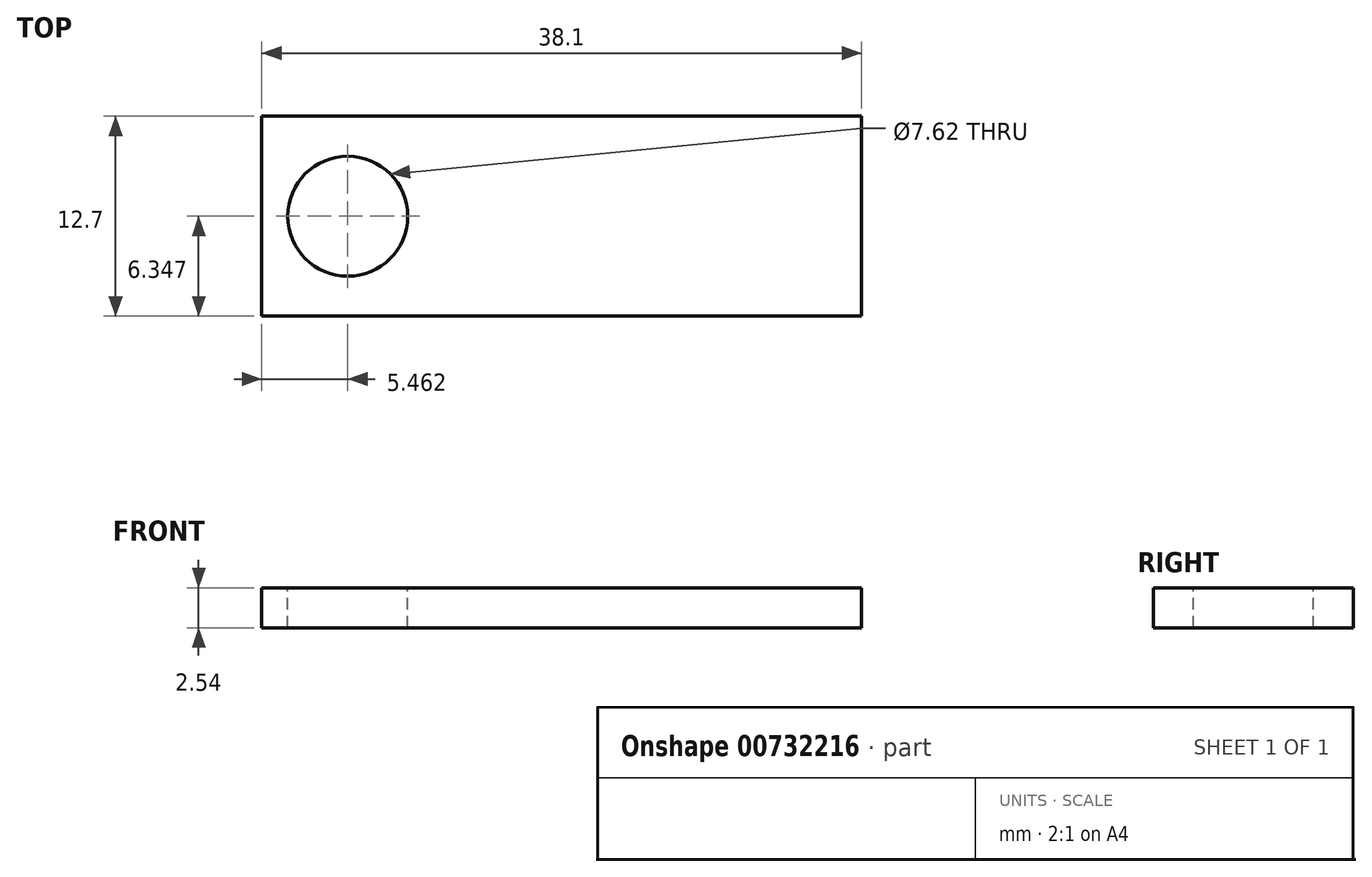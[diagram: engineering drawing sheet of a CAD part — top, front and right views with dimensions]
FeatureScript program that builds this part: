
annotation { "Feature Type Name" : "Feature", "Feature Type Description" : "" }
export const myFeature = defineFeature(function(context is Context, id is Id, definition is map)
    precondition{}
    {
        {
            var Q0;
            Q0=qCreatedBy(makeId("Top.planeOp"),FACE);
            var sketch = newSketch(context, id + "F0", { "sketchPlane" : qUnion([Q0])});
            skLineSegment(sketch, "E0", {"start": v(-135.86, 28.64) * mm, "end": v(-97.76, 28.64) * mm});
            skLineSegment(sketch, "E1", {"start": v(-135.86, 28.64) * mm, "end": v(-135.86, 15.94) * mm});
            skLineSegment(sketch, "E2", {"start": v(-135.86, 15.94) * mm, "end": v(-97.76, 15.94) * mm});
            skLineSegment(sketch, "E3", {"start": v(-97.76, 15.94) * mm, "end": v(-97.76, 28.64) * mm});
            skSolve(sketch);
        }
        {
            var Q0;
            Q0=makeQuery(id+"F0.imprint","IMPRINT",FACE,{"disambiguationData":[TD([[makeQuery(id+"F0.imprint","IMPRINT",EDGE,{"derivedFrom":sQuery(id+"F0.wireOp",EDGE,"E0")}),-1.0]])]});
            extrude(context, id + "F1", {"entities" : qUnion([Q0]), "depth" : 2.54 * mm, "offsetDistance" : 25.4 * mm});
        }
        {
            var Q0;
            Q0=makeQuery(id+"F1.opExtrude","CAP_FACE",FACE,{"disambiguationData":[OSD([sQuery(id+"F0.wireOp",EDGE,"E0"),sQuery(id+"F0.wireOp",EDGE,"E1"),sQuery(id+"F0.wireOp",EDGE,"E2"),sQuery(id+"F0.wireOp",EDGE,"E3")])],"isStart":false});
            var sketch = newSketch(context, id + "F2", { "sketchPlane" : qUnion([Q0])});
            skCircle(sketch, "E4", {"center": v(-130.4, 22.29) * mm, "radius": 3.81 * mm});
            skPoint(sketch, "E4.centerSnap0", {"position": v(-135.86, 22.29) * mm});
            skPoint(sketch, "E4.perimeterSnap0", {"position": v(-135.86, 22.29) * mm});
            skPoint(sketch, "E4.perimeterSnap1", {"position": v(-116.8, 15.94) * mm});
            skSolve(sketch);
        }
        {
            var Q0;
            Q0=makeQuery(id+"F2.imprint","IMPRINT",FACE,{"disambiguationData":[TD([[makeQuery(id+"F2.imprint","IMPRINT",EDGE,{"derivedFrom":sQuery(id+"F2.wireOp",EDGE,"E4")}),1.0]])]});
            var Q1;
            Q1=sQuery(id+"F2.wireOp",EDGE,"E4");
            extrude(context, id + "F3", {"entities" : qUnion([Q0]), "operationType" : NewBodyOperationType.REMOVE, "surfaceEntities" : qUnion([Q1]), "oppositeDirection" : true, "depth" : 25.4 * mm, "offsetDistance" : 25.4 * mm});
        }
        {
            var Q0;
            Q0=makeQuery(id+"F1.opExtrude","CAP_FACE",FACE,{"disambiguationData":[OSD([sQuery(id+"F0.wireOp",EDGE,"E0"),sQuery(id+"F0.wireOp",EDGE,"E1"),sQuery(id+"F0.wireOp",EDGE,"E2"),sQuery(id+"F0.wireOp",EDGE,"E3")])],"isStart":false});
            var sketch = newSketch(context, id + "F4", { "sketchPlane" : qUnion([Q0])});
            skText(sketch, "E5", { "text": "Josh", "fontName": "OpenSans-Regular.ttf"});
            const initialGuessF4  = {"E5": [-0.1234, 0.01914, 1, 0, 0.00604]};
            skSetInitialGuess(sketch, initialGuessF4);
            skSolve(sketch);
        }
        {
            var Q0;
            Q0 = qSketchRegion(id + "F4", true);
            extrude(context, id + "F5", {"entities" : qUnion([Q0]), "operationType" : NewBodyOperationType.ADD, "oppositeDirection" : true, "depth" : 1.27 * mm, "offsetDistance" : 25.4 * mm});
        }
    });
